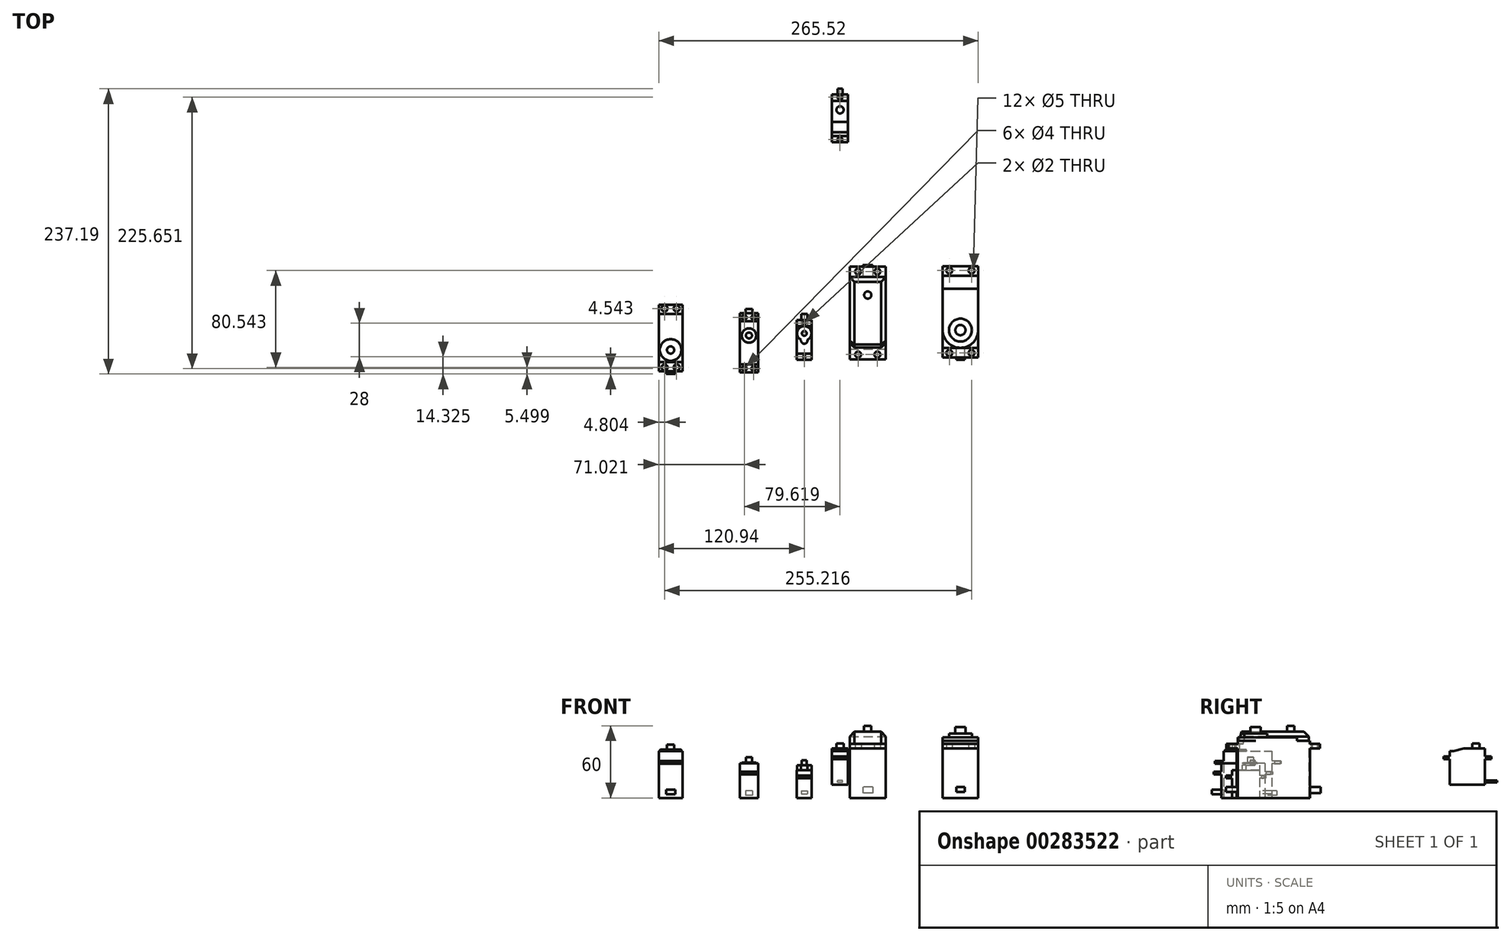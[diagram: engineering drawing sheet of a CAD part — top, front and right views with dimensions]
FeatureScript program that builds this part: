
annotation { "Feature Type Name" : "Feature", "Feature Type Description" : "" }
export const myFeature = defineFeature(function(context is Context, id is Id, definition is map)
    precondition{}
    {
        {
            var Q0;
            Q0=qCreatedBy(makeId("Top.planeOp"),FACE);
            var sketch = newSketch(context, id + "F0", { "sketchPlane" : qUnion([Q0])});
            skLineSegment(sketch, "E0.bottom", {"start": v(-143.99, -81.33) * mm, "end": v(-124.39, -81.33) * mm});
            skLineSegment(sketch, "E0.top", {"start": v(-143.99, -41.28) * mm, "end": v(-124.39, -41.28) * mm});
            skLineSegment(sketch, "E0.left", {"start": v(-143.99, -81.33) * mm, "end": v(-143.99, -41.28) * mm});
            skLineSegment(sketch, "E0.right", {"start": v(-124.39, -81.33) * mm, "end": v(-124.39, -41.28) * mm});
            skSolve(sketch);
        }
        {
            var Q0;
            Q0=makeQuery(id+"F0.imprint","IMPRINT",FACE,{"disambiguationData":[TD([[makeQuery(id+"F0.imprint","IMPRINT",EDGE,{"derivedFrom":sQuery(id+"F0.wireOp",EDGE,"E0.bottom")}),1.0]])]});
            extrude(context, id + "F1", {"entities" : qUnion([Q0]), "depth" : 28.3 * mm});
        }
        {
            var Q0;
            Q0=makeQuery(id+"F1.opExtrude","CAP_FACE",FACE,{"disambiguationData":[OSD([sQuery(id+"F0.wireOp",EDGE,"E0.bottom"),sQuery(id+"F0.wireOp",EDGE,"E0.top"),sQuery(id+"F0.wireOp",EDGE,"E0.left"),sQuery(id+"F0.wireOp",EDGE,"E0.right")])],"isStart":false});
            var sketch = newSketch(context, id + "F2", { "sketchPlane" : qUnion([Q0])});
            skLineSegment(sketch, "E1.bottom", {"start": v(-143.99, -33.78) * mm, "end": v(-124.39, -33.78) * mm});
            skLineSegment(sketch, "E1.top", {"start": v(-143.99, -88.83) * mm, "end": v(-124.39, -88.83) * mm});
            skLineSegment(sketch, "E1.left", {"start": v(-143.99, -33.78) * mm, "end": v(-143.99, -88.83) * mm});
            skLineSegment(sketch, "E1.right", {"start": v(-124.39, -33.78) * mm, "end": v(-124.39, -88.83) * mm});
            skCircle(sketch, "E2", {"center": v(-139.19, -36.78) * mm, "radius": 2.5 * mm});
            skCircle(sketch, "E3", {"center": v(-129.19, -36.78) * mm, "radius": 2.5 * mm});
            skCircle(sketch, "E4", {"center": v(-139.19, -85.83) * mm, "radius": 2.5 * mm});
            skCircle(sketch, "E5", {"center": v(-129.19, -85.83) * mm, "radius": 2.5 * mm});
            skLineSegment(sketch, "E6", {"start": v(-139.19, -85.83) * mm, "end": v(-129.19, -85.83) * mm, "construction": true});
            skLineSegment(sketch, "E7", {"start": v(-139.19, -36.78) * mm, "end": v(-129.19, -36.78) * mm, "construction": true});
            skLineSegment(sketch, "E8", {"start": v(-134.19, -36.78) * mm, "end": v(-134.19, -41.28) * mm, "construction": true});
            skLineSegment(sketch, "E9", {"start": v(-134.19, -85.83) * mm, "end": v(-134.19, -81.33) * mm, "construction": true});
            skSolve(sketch);
        }
        {
            var Q0;
            {var subQ1=makeQuery(id+"F1.opExtrude","CAP_EDGE",EDGE,{"disambiguationData":[OSD([sQuery(id+"F0.wireOp",EDGE,"E0.bottom")])],"isStart":false});Q0=makeQuery(id+"F2.imprint","IMPRINT",FACE,{"disambiguationData":[TD([[makeQuery(id+"F2.imprint","IMPRINT",EDGE,{"derivedFrom":subQ1}),1.0]])]});}
            extrude(context, id + "F3", {"entities" : qUnion([Q0]), "operationType" : NewBodyOperationType.ADD, "depth" : 10.5 * mm});
        }
        {
            var Q0;
            {var subQ2=sQuery(id+"F2.wireOp",EDGE,"E1.bottom");Q0=makeQuery(id+"F2.imprint","IMPRINT",FACE,{"disambiguationData":[TD([[makeQuery(id+"F2.imprint","IMPRINT",EDGE,{"derivedFrom":subQ2}),-1.0]])]});}
            var Q1;
            {var subQ2=sQuery(id+"F2.wireOp",EDGE,"E1.top");Q1=makeQuery(id+"F2.imprint","IMPRINT",FACE,{"disambiguationData":[TD([[makeQuery(id+"F2.imprint","IMPRINT",EDGE,{"derivedFrom":subQ2}),1.0]])]});}
            extrude(context, id + "F4", {"entities" : qUnion([Q0, Q1]), "operationType" : NewBodyOperationType.ADD, "depth" : 2.5 * mm});
        }
        {
            var Q0;
            Q0=makeQuery(id+"F3.opExtrude","CAP_FACE",FACE,{"disambiguationData":[OSD([sQuery(id+"F0.wireOp",EDGE,"E0.bottom"),sQuery(id+"F0.wireOp",EDGE,"E0.top"),sQuery(id+"F2.wireOp",EDGE,"E1.left"),sQuery(id+"F2.wireOp",EDGE,"E1.right")])],"isStart":false});
            var sketch = newSketch(context, id + "F5", { "sketchPlane" : qUnion([Q0])});
            skCircle(sketch, "E10", {"center": v(-134.19, -71.33) * mm, "radius": 9 * mm});
            skLineSegment(sketch, "E11", {"start": v(-134.19, -71.33) * mm, "end": v(-134.19, -81.33) * mm, "construction": true});
            skSolve(sketch);
        }
        {
            var Q0;
            Q0=makeQuery(id+"F5.imprint","IMPRINT",FACE,{"disambiguationData":[TD([[makeQuery(id+"F5.imprint","IMPRINT",EDGE,{"derivedFrom":sQuery(id+"F5.wireOp",EDGE,"E10")}),1.0]])]});
            extrude(context, id + "F6", {"entities" : qUnion([Q0]), "operationType" : NewBodyOperationType.ADD, "depth" : 1.5 * mm});
        }
        {
            var Q0;
            Q0=makeQuery(id+"F6.opExtrude","CAP_EDGE",EDGE,{"disambiguationData":[OSD([sQuery(id+"F5.wireOp",EDGE,"E10")])],"isStart":false});
            fillet(context, id + "F7", {"entities" : qUnion([Q0]), "radius" : 1 * mm, "tangentPropagation" : true, "allowEdgeOverflow" : false});
        }
        {
            var Q0;
            Q0=makeQuery(id+"F6.opExtrude","CAP_FACE",FACE,{"disambiguationData":[OSD([sQuery(id+"F5.wireOp",EDGE,"E10")])],"isStart":false});
            var sketch = newSketch(context, id + "F8", { "sketchPlane" : qUnion([Q0])});
            skCircle(sketch, "E12", {"center": v(-134.19, -71.33) * mm, "radius": 3 * mm});
            skSolve(sketch);
        }
        {
            var Q0;
            Q0=makeQuery(id+"F8.imprint","IMPRINT",FACE,{"disambiguationData":[TD([[makeQuery(id+"F8.imprint","IMPRINT",EDGE,{"derivedFrom":sQuery(id+"F8.wireOp",EDGE,"E12")}),1.0]])]});
            extrude(context, id + "F9", {"entities" : qUnion([Q0]), "operationType" : NewBodyOperationType.ADD, "depth" : 4 * mm});
        }
        {
            var Q0;
            {var subQ1=sQuery(id+"F0.wireOp",EDGE,"E0.right");var subQ2=sQuery(id+"F0.wireOp",EDGE,"E0.left");var subQ3=sQuery(id+"F0.wireOp",EDGE,"E0.top");var subQ4=sQuery(id+"F0.wireOp",EDGE,"E0.bottom");Q0=makeQuery(id+"F4.boolean.opBoolean","SPLIT",FACE,{"disambiguationData":[TD([makeQuery(id+"F1.opExtrude","CAP_FACE",FACE,{"disambiguationData":[OSD([subQ4,subQ3,subQ2,subQ1])],"isStart":true})])],"derivedFrom":makeQuery(id+"F3.boolean.opBoolean","MERGE",FACE,{"derivedFrom":[makeQuery(id+"F1.opExtrude","SWEPT_FACE",FACE,{"disambiguationData":[OSD([subQ4])]}),makeQuery(id+"F3.opExtrude","SWEPT_FACE",FACE,{"disambiguationData":[OSD([subQ4])]})]})});}
            var sketch = newSketch(context, id + "F10", { "sketchPlane" : qUnion([Q0])});
            skLineSegment(sketch, "E13.bottom", {"start": v(-137.94, 7) * mm, "end": v(-130.44, 7) * mm});
            skLineSegment(sketch, "E13.top", {"start": v(-137.94, 3) * mm, "end": v(-130.44, 3) * mm});
            skLineSegment(sketch, "E13.left", {"start": v(-137.94, 7) * mm, "end": v(-137.94, 3) * mm});
            skLineSegment(sketch, "E13.right", {"start": v(-130.44, 7) * mm, "end": v(-130.44, 3) * mm});
            skLineSegment(sketch, "E14", {"start": v(-134.19, 0) * mm, "end": v(-134.19, 3) * mm, "construction": true});
            skSolve(sketch);
        }
        {
            var Q0;
            Q0=makeQuery(id+"F10.imprint","IMPRINT",FACE,{"disambiguationData":[TD([[makeQuery(id+"F10.imprint","IMPRINT",EDGE,{"derivedFrom":sQuery(id+"F10.wireOp",EDGE,"E13.bottom")}),-1.0]])]});
            extrude(context, id + "F11", {"entities" : qUnion([Q0]), "operationType" : NewBodyOperationType.ADD, "depth" : 10 * mm});
        }
        {
            var Q0;
            Q0=qCreatedBy(makeId("Top.planeOp"),FACE);
            var sketch = newSketch(context, id + "F12", { "sketchPlane" : qUnion([Q0])});
            skLineSegment(sketch, "E15.bottom", {"start": v(-76.77, -47.29) * mm, "end": v(-61.27, -47.29) * mm});
            skLineSegment(sketch, "E15.top", {"start": v(-76.77, -83.29) * mm, "end": v(-61.27, -83.29) * mm});
            skLineSegment(sketch, "E15.left", {"start": v(-76.77, -47.29) * mm, "end": v(-76.77, -83.29) * mm});
            skLineSegment(sketch, "E15.right", {"start": v(-61.27, -47.29) * mm, "end": v(-61.27, -83.29) * mm});
            skSolve(sketch);
        }
        {
            var Q0;
            Q0=makeQuery(id+"F12.imprint","IMPRINT",FACE,{"disambiguationData":[TD([[makeQuery(id+"F12.imprint","IMPRINT",EDGE,{"derivedFrom":sQuery(id+"F12.wireOp",EDGE,"E15.bottom")}),-1.0]])]});
            extrude(context, id + "F13", {"entities" : qUnion([Q0]), "depth" : 19.5 * mm});
        }
        {
            var Q0;
            Q0=makeQuery(id+"F13.opExtrude","CAP_FACE",FACE,{"disambiguationData":[OSD([sQuery(id+"F12.wireOp",EDGE,"E15.bottom"),sQuery(id+"F12.wireOp",EDGE,"E15.top"),sQuery(id+"F12.wireOp",EDGE,"E15.left"),sQuery(id+"F12.wireOp",EDGE,"E15.right")])],"isStart":false});
            var sketch = newSketch(context, id + "F14", { "sketchPlane" : qUnion([Q0])});
            skLineSegment(sketch, "E16", {"start": v(-76.77, -47.29) * mm, "end": v(-76.77, -40.79) * mm});
            skLineSegment(sketch, "E17", {"start": v(-61.27, -47.29) * mm, "end": v(-61.27, -40.79) * mm});
            skLineSegment(sketch, "E18", {"start": v(-76.77, -40.79) * mm, "end": v(-61.27, -40.79) * mm});
            skLineSegment(sketch, "E19", {"start": v(-76.77, -83.29) * mm, "end": v(-76.77, -89.79) * mm});
            skLineSegment(sketch, "E20", {"start": v(-61.27, -83.29) * mm, "end": v(-61.27, -89.79) * mm});
            skLineSegment(sketch, "E21", {"start": v(-61.27, -89.79) * mm, "end": v(-76.77, -89.79) * mm});
            skCircle(sketch, "E22", {"center": v(-72.97, -44.29) * mm, "radius": 2 * mm});
            skCircle(sketch, "E23", {"center": v(-65.07, -44.29) * mm, "radius": 2 * mm});
            skCircle(sketch, "E24", {"center": v(-65.07, -86.79) * mm, "radius": 2 * mm});
            skCircle(sketch, "E25", {"center": v(-72.97, -86.79) * mm, "radius": 2 * mm});
            skLineSegment(sketch, "E26", {"start": v(-76.77, -44.29) * mm, "end": v(-61.27, -44.29) * mm, "construction": true});
            skLineSegment(sketch, "E27", {"start": v(-72.97, -40.79) * mm, "end": v(-72.97, -47.29) * mm, "construction": true});
            skLineSegment(sketch, "E28", {"start": v(-65.07, -40.79) * mm, "end": v(-65.07, -47.29) * mm, "construction": true});
            skLineSegment(sketch, "E29", {"start": v(-76.77, -86.79) * mm, "end": v(-61.27, -86.79) * mm, "construction": true});
            skLineSegment(sketch, "E30", {"start": v(-72.97, -83.29) * mm, "end": v(-72.97, -89.79) * mm, "construction": true});
            skLineSegment(sketch, "E31", {"start": v(-65.07, -83.29) * mm, "end": v(-65.07, -89.79) * mm, "construction": true});
            skSolve(sketch);
        }
        {
            var Q0;
            Q0=makeQuery(id+"F14.imprint","IMPRINT",FACE,{"disambiguationData":[TD([[makeQuery(id+"F14.imprint","IMPRINT",EDGE,{"derivedFrom":makeQuery(id+"F13.opExtrude","CAP_EDGE",EDGE,{"disambiguationData":[OSD([sQuery(id+"F12.wireOp",EDGE,"E15.bottom")])],"isStart":false})}),-1.0]])]});
            var Q1;
            Q1=makeQuery(id+"F14.imprint","IMPRINT",FACE,{"disambiguationData":[TD([[makeQuery(id+"F14.imprint","IMPRINT",EDGE,{"derivedFrom":sQuery(id+"F14.wireOp",EDGE,"E19")}),1.0]])]});
            var Q2;
            Q2=makeQuery(id+"F14.imprint","IMPRINT",FACE,{"disambiguationData":[TD([[makeQuery(id+"F14.imprint","IMPRINT",EDGE,{"derivedFrom":sQuery(id+"F14.wireOp",EDGE,"E16")}),-1.0]])]});
            extrude(context, id + "F15", {"entities" : qUnion([Q0, Q1, Q2]), "operationType" : NewBodyOperationType.ADD, "depth" : 2.4 * mm});
        }
        {
            var Q0;
            Q0=makeQuery(id+"F15.opExtrude","CAP_FACE",FACE,{"disambiguationData":[OSD([sQuery(id+"F12.wireOp",EDGE,"E15.left"),sQuery(id+"F12.wireOp",EDGE,"E15.right"),sQuery(id+"F14.wireOp",EDGE,"E16"),sQuery(id+"F14.wireOp",EDGE,"E17"),sQuery(id+"F14.wireOp",EDGE,"E18"),sQuery(id+"F14.wireOp",EDGE,"E19"),sQuery(id+"F14.wireOp",EDGE,"E20"),sQuery(id+"F14.wireOp",EDGE,"E21"),sQuery(id+"F14.wireOp",EDGE,"E22"),sQuery(id+"F14.wireOp",EDGE,"E23"),sQuery(id+"F14.wireOp",EDGE,"E24"),sQuery(id+"F14.wireOp",EDGE,"E25")])],"isStart":false});
            var sketch = newSketch(context, id + "F16", { "sketchPlane" : qUnion([Q0])});
            skLineSegment(sketch, "E32", {"start": v(-76.77, -83.29) * mm, "end": v(-61.27, -83.29) * mm});
            skLineSegment(sketch, "E33", {"start": v(-61.27, -47.29) * mm, "end": v(-76.77, -47.29) * mm});
            skSolve(sketch);
        }
        {
            var Q0;
            {var subQ0=sQuery(id+"F16.wireOp",EDGE,"E32");Q0=makeQuery(id+"F16.imprint","IMPRINT",FACE,{"disambiguationData":[TD([[makeQuery(id+"F16.imprint","IMPRINT",EDGE,{"derivedFrom":subQ0}),1.0]])]});}
            extrude(context, id + "F17", {"entities" : qUnion([Q0]), "operationType" : NewBodyOperationType.ADD, "depth" : 7 * mm});
        }
        {
            var Q0;
            Q0=makeQuery(id+"F17.opExtrude","CAP_FACE",FACE,{"disambiguationData":[OSD([sQuery(id+"F12.wireOp",EDGE,"E15.left"),sQuery(id+"F12.wireOp",EDGE,"E15.right"),sQuery(id+"F14.wireOp",EDGE,"E16"),sQuery(id+"F14.wireOp",EDGE,"E17"),sQuery(id+"F14.wireOp",EDGE,"E19"),sQuery(id+"F14.wireOp",EDGE,"E20"),sQuery(id+"F16.wireOp",EDGE,"E32"),sQuery(id+"F16.wireOp",EDGE,"E33")])],"isStart":false});
            var sketch = newSketch(context, id + "F18", { "sketchPlane" : qUnion([Q0])});
            skCircle(sketch, "E34", {"center": v(-69.02, -59.29) * mm, "radius": 6 * mm});
            skLineSegment(sketch, "E35", {"start": v(-69.02, -47.29) * mm, "end": v(-69.02, -59.29) * mm, "construction": true});
            skSolve(sketch);
        }
        {
            var Q0;
            Q0=makeQuery(id+"F18.imprint","IMPRINT",FACE,{"disambiguationData":[TD([[makeQuery(id+"F18.imprint","IMPRINT",EDGE,{"derivedFrom":sQuery(id+"F18.wireOp",EDGE,"E34")}),1.0]])]});
            extrude(context, id + "F19", {"entities" : qUnion([Q0]), "operationType" : NewBodyOperationType.ADD, "depth" : 0.65 * mm});
        }
        {
            var Q0;
            Q0=makeQuery(id+"F19.opExtrude","CAP_EDGE",EDGE,{"disambiguationData":[OSD([sQuery(id+"F18.wireOp",EDGE,"E34")])],"isStart":false});
            fillet(context, id + "F20", {"entities" : qUnion([Q0]), "radius" : 1 * mm, "tangentPropagation" : true, "allowEdgeOverflow" : false});
        }
        {
            var Q0;
            Q0=makeQuery(id+"F19.opExtrude","CAP_FACE",FACE,{"disambiguationData":[OSD([sQuery(id+"F18.wireOp",EDGE,"E34")])],"isStart":false});
            var sketch = newSketch(context, id + "F21", { "sketchPlane" : qUnion([Q0])});
            skCircle(sketch, "E36", {"center": v(-69.02, -59.29) * mm, "radius": 2.5 * mm});
            skSolve(sketch);
        }
        {
            var Q0;
            Q0=makeQuery(id+"F21.imprint","IMPRINT",FACE,{"disambiguationData":[TD([[makeQuery(id+"F21.imprint","IMPRINT",EDGE,{"derivedFrom":sQuery(id+"F21.wireOp",EDGE,"E36")}),1.0]])]});
            extrude(context, id + "F22", {"entities" : qUnion([Q0]), "operationType" : NewBodyOperationType.ADD, "depth" : 4.2 * mm});
        }
        {
            var Q0;
            Q0=makeQuery(id+"F13.opExtrude","SWEPT_FACE",FACE,{"disambiguationData":[OSD([sQuery(id+"F12.wireOp",EDGE,"E15.bottom")])]});
            var sketch = newSketch(context, id + "F23", { "sketchPlane" : qUnion([Q0])});
            skLineSegment(sketch, "E37.bottom", {"start": v(66.02, 6) * mm, "end": v(72.02, 6) * mm});
            skLineSegment(sketch, "E37.top", {"start": v(66.02, 2) * mm, "end": v(72.02, 2) * mm});
            skLineSegment(sketch, "E37.left", {"start": v(66.02, 6) * mm, "end": v(66.02, 2) * mm});
            skLineSegment(sketch, "E37.right", {"start": v(72.02, 6) * mm, "end": v(72.02, 2) * mm});
            skLineSegment(sketch, "E38", {"start": v(69.02, 0) * mm, "end": v(69.02, 6) * mm, "construction": true});
            skSolve(sketch);
        }
        {
            var Q0;
            Q0=makeQuery(id+"F23.imprint","IMPRINT",FACE,{"disambiguationData":[TD([[makeQuery(id+"F23.imprint","IMPRINT",EDGE,{"derivedFrom":sQuery(id+"F23.wireOp",EDGE,"E37.bottom")}),-1.0]])]});
            extrude(context, id + "F24", {"entities" : qUnion([Q0]), "operationType" : NewBodyOperationType.ADD, "depth" : 10 * mm});
        }
        {
            var Q0;
            Q0=qCreatedBy(makeId("Top.planeOp"),FACE);
            var sketch = newSketch(context, id + "F25", { "sketchPlane" : qUnion([Q0])});
            skLineSegment(sketch, "E39.bottom", {"start": v(-29.3, -74.5) * mm, "end": v(-16.8, -74.5) * mm});
            skLineSegment(sketch, "E39.top", {"start": v(-29.3, -51.5) * mm, "end": v(-16.8, -51.5) * mm});
            skLineSegment(sketch, "E39.left", {"start": v(-29.3, -74.5) * mm, "end": v(-29.3, -51.5) * mm});
            skLineSegment(sketch, "E39.right", {"start": v(-16.8, -74.5) * mm, "end": v(-16.8, -51.5) * mm});
            skSolve(sketch);
        }
        {
            var Q0;
            Q0=makeQuery(id+"F25.imprint","IMPRINT",FACE,{"disambiguationData":[TD([[makeQuery(id+"F25.imprint","IMPRINT",EDGE,{"derivedFrom":sQuery(id+"F25.wireOp",EDGE,"E39.bottom")}),1.0]])]});
            extrude(context, id + "F26", {"entities" : qUnion([Q0]), "depth" : 16.5 * mm});
        }
        {
            var Q0;
            Q0=makeQuery(id+"F26.opExtrude","CAP_FACE",FACE,{"disambiguationData":[OSD([sQuery(id+"F25.wireOp",EDGE,"E39.bottom"),sQuery(id+"F25.wireOp",EDGE,"E39.top"),sQuery(id+"F25.wireOp",EDGE,"E39.left"),sQuery(id+"F25.wireOp",EDGE,"E39.right")])],"isStart":false});
            var sketch = newSketch(context, id + "F27", { "sketchPlane" : qUnion([Q0])});
            skLineSegment(sketch, "E40", {"start": v(-29.3, -51.5) * mm, "end": v(-29.3, -46.5) * mm});
            skLineSegment(sketch, "E41", {"start": v(-29.3, -46.5) * mm, "end": v(-16.8, -46.5) * mm});
            skLineSegment(sketch, "E42", {"start": v(-16.8, -46.5) * mm, "end": v(-16.8, -51.5) * mm});
            skLineSegment(sketch, "E43", {"start": v(-29.3, -74.5) * mm, "end": v(-29.3, -79.5) * mm});
            skLineSegment(sketch, "E44", {"start": v(-29.3, -79.5) * mm, "end": v(-16.8, -79.5) * mm});
            skLineSegment(sketch, "E45", {"start": v(-16.8, -79.5) * mm, "end": v(-16.8, -74.5) * mm});
            skLineSegment(sketch, "E46", {"start": v(-29.3, -49) * mm, "end": v(-16.8, -49) * mm, "construction": true});
            skLineSegment(sketch, "E47", {"start": v(-23.05, -49) * mm, "end": v(-23.05, -46.5) * mm, "construction": true});
            skLineSegment(sketch, "E48", {"start": v(-29.3, -77) * mm, "end": v(-16.8, -77) * mm, "construction": true});
            skLineSegment(sketch, "E49", {"start": v(-23.05, -77) * mm, "end": v(-23.05, -79.5) * mm, "construction": true});
            skCircle(sketch, "E50", {"center": v(-23.05, -49) * mm, "radius": 1 * mm});
            skCircle(sketch, "E51", {"center": v(-23.05, -77) * mm, "radius": 1 * mm});
            skSolve(sketch);
        }
        {
            var Q0;
            Q0=makeQuery(id+"F27.imprint","IMPRINT",FACE,{"disambiguationData":[TD([[makeQuery(id+"F27.imprint","IMPRINT",EDGE,{"derivedFrom":sQuery(id+"F27.wireOp",EDGE,"E43")}),1.0]])]});
            var Q1;
            Q1=makeQuery(id+"F27.imprint","IMPRINT",FACE,{"disambiguationData":[TD([[makeQuery(id+"F27.imprint","IMPRINT",EDGE,{"derivedFrom":makeQuery(id+"F26.opExtrude","CAP_EDGE",EDGE,{"disambiguationData":[OSD([sQuery(id+"F25.wireOp",EDGE,"E39.bottom")])],"isStart":false})}),1.0]])]});
            var Q2;
            Q2=makeQuery(id+"F27.imprint","IMPRINT",FACE,{"disambiguationData":[TD([[makeQuery(id+"F27.imprint","IMPRINT",EDGE,{"derivedFrom":sQuery(id+"F27.wireOp",EDGE,"E40")}),-1.0]])]});
            extrude(context, id + "F28", {"entities" : qUnion([Q0, Q1, Q2]), "operationType" : NewBodyOperationType.ADD, "depth" : 2.2 * mm});
        }
        {
            var Q0;
            Q0=makeQuery(id+"F28.opExtrude","CAP_FACE",FACE,{"disambiguationData":[OSD([sQuery(id+"F25.wireOp",EDGE,"E39.left"),sQuery(id+"F25.wireOp",EDGE,"E39.right"),sQuery(id+"F27.wireOp",EDGE,"E40"),sQuery(id+"F27.wireOp",EDGE,"E41"),sQuery(id+"F27.wireOp",EDGE,"E42"),sQuery(id+"F27.wireOp",EDGE,"E43"),sQuery(id+"F27.wireOp",EDGE,"E44"),sQuery(id+"F27.wireOp",EDGE,"E45"),sQuery(id+"F27.wireOp",EDGE,"E50"),sQuery(id+"F27.wireOp",EDGE,"E51")])],"isStart":false});
            var sketch = newSketch(context, id + "F29", { "sketchPlane" : qUnion([Q0])});
            skLineSegment(sketch, "E52", {"start": v(-29.3, -51.5) * mm, "end": v(-16.8, -51.5) * mm});
            skLineSegment(sketch, "E53", {"start": v(-16.8, -74.5) * mm, "end": v(-29.3, -74.5) * mm});
            skSolve(sketch);
        }
        {
            var Q0;
            {var subQ0=sQuery(id+"F29.wireOp",EDGE,"E52");Q0=makeQuery(id+"F29.imprint","IMPRINT",FACE,{"disambiguationData":[TD([[makeQuery(id+"F29.imprint","IMPRINT",EDGE,{"derivedFrom":subQ0}),-1.0]])]});}
            extrude(context, id + "F30", {"entities" : qUnion([Q0]), "operationType" : NewBodyOperationType.ADD, "depth" : 4.5 * mm});
        }
        {
            var Q0;
            Q0=makeQuery(id+"F30.opExtrude","CAP_FACE",FACE,{"disambiguationData":[OSD([sQuery(id+"F25.wireOp",EDGE,"E39.left"),sQuery(id+"F25.wireOp",EDGE,"E39.right"),sQuery(id+"F27.wireOp",EDGE,"E40"),sQuery(id+"F27.wireOp",EDGE,"E42"),sQuery(id+"F27.wireOp",EDGE,"E43"),sQuery(id+"F27.wireOp",EDGE,"E45"),sQuery(id+"F29.wireOp",EDGE,"E52"),sQuery(id+"F29.wireOp",EDGE,"E53")])],"isStart":false});
            var sketch = newSketch(context, id + "F31", { "sketchPlane" : qUnion([Q0])});
            skArc(sketch, "E54", {"start": v(-20.47, -62.92) * mm, "mid": v(-23.05, -51.5) * mm, "end": v(-25.63, -62.92) * mm});
            skLineSegment(sketch, "E55", {"start": v(-23.05, -57.5) * mm, "end": v(-23.05, -51.5) * mm, "construction": true});
            skLineSegment(sketch, "E56", {"start": v(-23.05, -57.5) * mm, "end": v(-23.05, -63.5) * mm, "construction": true});
            skArc(sketch, "E57", {"start": v(-25.63, -62.92) * mm, "mid": v(-23.05, -66.16) * mm, "end": v(-20.47, -62.92) * mm});
            skSolve(sketch);
        }
        {
            var Q0;
            {var subQ0=sQuery(id+"F31.wireOp",EDGE,"E57");Q0=makeQuery(id+"F31.imprint","IMPRINT",FACE,{"disambiguationData":[TD([[makeQuery(id+"F31.imprint","IMPRINT",EDGE,{"derivedFrom":subQ0}),1.0]])]});}
            extrude(context, id + "F32", {"entities" : qUnion([Q0]), "operationType" : NewBodyOperationType.ADD, "depth" : 4 * mm});
        }
        {
            var Q0;
            Q0=makeQuery(id+"F32.opExtrude","CAP_FACE",FACE,{"disambiguationData":[OSD([sQuery(id+"F31.wireOp",EDGE,"E54"),sQuery(id+"F31.wireOp",EDGE,"E57")])],"isStart":false});
            var sketch = newSketch(context, id + "F33", { "sketchPlane" : qUnion([Q0])});
            skCircle(sketch, "E58", {"center": v(-23.05, -57.5) * mm, "radius": 2 * mm});
            skSolve(sketch);
        }
        {
            var Q0;
            Q0=makeQuery(id+"F33.imprint","IMPRINT",FACE,{"disambiguationData":[TD([[makeQuery(id+"F33.imprint","IMPRINT",EDGE,{"derivedFrom":sQuery(id+"F33.wireOp",EDGE,"E58")}),1.0]])]});
            extrude(context, id + "F34", {"entities" : qUnion([Q0]), "operationType" : NewBodyOperationType.ADD, "depth" : 4 * mm});
        }
        {
            var Q0;
            Q0=makeQuery(id+"F26.opExtrude","SWEPT_FACE",FACE,{"disambiguationData":[OSD([sQuery(id+"F25.wireOp",EDGE,"E39.top")])]});
            var sketch = newSketch(context, id + "F35", { "sketchPlane" : qUnion([Q0])});
            skLineSegment(sketch, "E59.bottom", {"start": v(25.55, 6) * mm, "end": v(20.55, 6) * mm});
            skLineSegment(sketch, "E59.top", {"start": v(25.55, 3.5) * mm, "end": v(20.55, 3.5) * mm});
            skLineSegment(sketch, "E59.left", {"start": v(25.55, 6) * mm, "end": v(25.55, 3.5) * mm});
            skLineSegment(sketch, "E59.right", {"start": v(20.55, 6) * mm, "end": v(20.55, 3.5) * mm});
            skLineSegment(sketch, "E60", {"start": v(23.05, 6) * mm, "end": v(23.05, 0) * mm, "construction": true});
            skSolve(sketch);
        }
        {
            var Q0;
            Q0=makeQuery(id+"F35.imprint","IMPRINT",FACE,{"disambiguationData":[TD([[makeQuery(id+"F35.imprint","IMPRINT",EDGE,{"derivedFrom":sQuery(id+"F35.wireOp",EDGE,"E59.bottom")}),1.0]])]});
            extrude(context, id + "F36", {"entities" : qUnion([Q0]), "operationType" : NewBodyOperationType.ADD, "depth" : 10 * mm});
        }
        {
            var Q0;
            Q0=qCreatedBy(makeId("Right.planeOp"),FACE);
            var sketch = newSketch(context, id + "F37", { "sketchPlane" : qUnion([Q0])});
            skLineSegment(sketch, "E61.bottom", {"start": v(106.66, 10.85) * mm, "end": v(135.86, 10.85) * mm});
            skLineSegment(sketch, "E61.top", {"start": v(118.36, 41.15) * mm, "end": v(135.86, 41.15) * mm});
            skLineSegment(sketch, "E61.left", {"start": v(106.66, 10.85) * mm, "end": v(106.66, 32.35) * mm});
            skLineSegment(sketch, "E61.right", {"start": v(135.86, 10.85) * mm, "end": v(135.86, 32.35) * mm});
            skLineSegment(sketch, "E62.bottom", {"start": v(135.86, 32.35) * mm, "end": v(141.11, 32.35) * mm});
            skLineSegment(sketch, "E62.top", {"start": v(135.86, 34.35) * mm, "end": v(141.11, 34.35) * mm});
            skLineSegment(sketch, "E62.right", {"start": v(141.11, 32.35) * mm, "end": v(141.11, 34.35) * mm});
            skLineSegment(sketch, "E63.bottom", {"start": v(106.66, 34.35) * mm, "end": v(101.41, 34.35) * mm});
            skLineSegment(sketch, "E63.top", {"start": v(106.66, 32.35) * mm, "end": v(101.41, 32.35) * mm});
            skLineSegment(sketch, "E63.right", {"start": v(101.41, 34.35) * mm, "end": v(101.41, 32.35) * mm});
            skLineSegment(sketch, "E64", {"start": v(135.86, 32.35) * mm, "end": v(106.66, 32.35) * mm, "construction": true});
            skLineSegment(sketch, "E65", {"start": v(106.66, 34.35) * mm, "end": v(135.86, 34.35) * mm, "construction": true});
            skLineSegment(sketch, "E66", {"start": v(106.66, 38.85) * mm, "end": v(109.66, 38.85) * mm});
            skLineSegment(sketch, "E67", {"start": v(109.66, 38.85) * mm, "end": v(118.36, 41.15) * mm});
            skLineSegment(sketch, "E68.trimOffspring", {"start": v(106.66, 34.35) * mm, "end": v(106.66, 38.85) * mm});
            skLineSegment(sketch, "E69.trimOffspring", {"start": v(135.86, 34.35) * mm, "end": v(135.86, 41.15) * mm});
            skSolve(sketch);
        }
        {
            var Q0;
            Q0=makeQuery(id+"F37.imprint","IMPRINT",FACE,{"disambiguationData":[TD([[makeQuery(id+"F37.imprint","IMPRINT",EDGE,{"derivedFrom":sQuery(id+"F37.wireOp",EDGE,"E61.bottom")}),1.0]])]});
            extrude(context, id + "F38", {"entities" : qUnion([Q0]), "depth" : 13.3 * mm});
        }
        {
            var Q0;
            Q0=makeQuery(id+"F38.opExtrude","SWEPT_FACE",FACE,{"disambiguationData":[OSD([sQuery(id+"F37.wireOp",EDGE,"E61.top")])]});
            var sketch = newSketch(context, id + "F39", { "sketchPlane" : qUnion([Q0])});
            skCircle(sketch, "E70", {"center": v(6.65, 128.36) * mm, "radius": 3 * mm});
            skLineSegment(sketch, "E71", {"start": v(6.65, 135.86) * mm, "end": v(6.65, 128.36) * mm, "construction": true});
            skSolve(sketch);
        }
        {
            var Q0;
            Q0=makeQuery(id+"F39.imprint","IMPRINT",FACE,{"disambiguationData":[TD([[makeQuery(id+"F39.imprint","IMPRINT",EDGE,{"derivedFrom":sQuery(id+"F39.wireOp",EDGE,"E70")}),1.0]])]});
            extrude(context, id + "F40", {"entities" : qUnion([Q0]), "operationType" : NewBodyOperationType.ADD, "depth" : 4 * mm});
        }
        {
            var Q0;
            Q0=makeQuery(id+"F38.opExtrude","SWEPT_FACE",FACE,{"disambiguationData":[OSD([sQuery(id+"F37.wireOp",EDGE,"E63.bottom")])]});
            var sketch = newSketch(context, id + "F41", { "sketchPlane" : qUnion([Q0])});
            skLineSegment(sketch, "E72", {"start": v(6.65, 101.41) * mm, "end": v(6.65, 106.66) * mm, "construction": true});
            skLineSegment(sketch, "E73", {"start": v(6.65, 141.11) * mm, "end": v(6.65, 136.02) * mm, "construction": true});
            skCircle(sketch, "E74", {"center": v(6.65, 138.86) * mm, "radius": 2 * mm});
            skCircle(sketch, "E75", {"center": v(6.65, 103.66) * mm, "radius": 2 * mm});
            skSolve(sketch);
        }
        {
            var Q0;
            Q0=makeQuery(id+"F41.imprint","IMPRINT",FACE,{"disambiguationData":[TD([[makeQuery(id+"F41.imprint","IMPRINT",EDGE,{"derivedFrom":sQuery(id+"F41.wireOp",EDGE,"E75")}),1.0]])]});
            var Q1;
            Q1=makeQuery(id+"F41.imprint","IMPRINT",FACE,{"disambiguationData":[TD([[makeQuery(id+"F41.imprint","IMPRINT",EDGE,{"derivedFrom":sQuery(id+"F41.wireOp",EDGE,"E74")}),1.0]])]});
            extrude(context, id + "F42", {"entities" : qUnion([Q0, Q1]), "operationType" : NewBodyOperationType.REMOVE, "endBound" : BoundingType.THROUGH_ALL, "oppositeDirection" : true, "depth" : 25 * mm});
        }
        {
            var Q0;
            Q0=makeQuery(id+"F38.opExtrude","SWEPT_FACE",FACE,{"disambiguationData":[OSD([sQuery(id+"F37.wireOp",EDGE,"E61.right")])]});
            var sketch = newSketch(context, id + "F43", { "sketchPlane" : qUnion([Q0])});
            skLineSegment(sketch, "E76.bottom", {"start": v(-8.65, 12.85) * mm, "end": v(-4.65, 12.85) * mm});
            skLineSegment(sketch, "E76.top", {"start": v(-8.65, 14.35) * mm, "end": v(-4.65, 14.35) * mm});
            skLineSegment(sketch, "E76.left", {"start": v(-8.65, 12.85) * mm, "end": v(-8.65, 14.35) * mm});
            skLineSegment(sketch, "E76.right", {"start": v(-4.65, 12.85) * mm, "end": v(-4.65, 14.35) * mm});
            skLineSegment(sketch, "E77", {"start": v(-6.65, 10.85) * mm, "end": v(-6.65, 12.85) * mm, "construction": true});
            skSolve(sketch);
        }
        {
            var Q0;
            Q0=makeQuery(id+"F43.imprint","IMPRINT",FACE,{"disambiguationData":[TD([[makeQuery(id+"F43.imprint","IMPRINT",EDGE,{"derivedFrom":sQuery(id+"F43.wireOp",EDGE,"E76.bottom")}),1.0]])]});
            extrude(context, id + "F44", {"entities" : qUnion([Q0]), "operationType" : NewBodyOperationType.ADD, "depth" : 10 * mm});
        }
        {
            var Q0;
            Q0=qCreatedBy(makeId("Top.planeOp"),FACE);
            var sketch = newSketch(context, id + "F45", { "sketchPlane" : qUnion([Q0])});
            skLineSegment(sketch, "E78.bottom", {"start": v(14.71, -70.64) * mm, "end": v(44.71, -70.64) * mm});
            skLineSegment(sketch, "E78.top", {"start": v(14.71, -10.64) * mm, "end": v(44.71, -10.64) * mm});
            skLineSegment(sketch, "E78.left", {"start": v(14.71, -70.64) * mm, "end": v(14.71, -10.64) * mm});
            skLineSegment(sketch, "E78.right", {"start": v(44.71, -70.64) * mm, "end": v(44.71, -10.64) * mm});
            skSolve(sketch);
        }
        {
            var Q0;
            Q0=makeQuery(id+"F45.imprint","IMPRINT",FACE,{"disambiguationData":[TD([[makeQuery(id+"F45.imprint","IMPRINT",EDGE,{"derivedFrom":sQuery(id+"F45.wireOp",EDGE,"E78.bottom")}),1.0]])]});
            extrude(context, id + "F46", {"entities" : qUnion([Q0]), "depth" : 41 * mm, "offsetDistance" : 25 * mm});
        }
        {
            var Q0;
            Q0=makeQuery(id+"F46.opExtrude","CAP_FACE",FACE,{"disambiguationData":[OSD([sQuery(id+"F45.wireOp",EDGE,"E78.bottom"),sQuery(id+"F45.wireOp",EDGE,"E78.top"),sQuery(id+"F45.wireOp",EDGE,"E78.left"),sQuery(id+"F45.wireOp",EDGE,"E78.right")])],"isStart":false});
            var sketch = newSketch(context, id + "F47", { "sketchPlane" : qUnion([Q0])});
            skLineSegment(sketch, "E79.bottom", {"start": v(14.71, -79.14) * mm, "end": v(44.71, -79.14) * mm});
            skLineSegment(sketch, "E79.top", {"start": v(14.71, -2.14) * mm, "end": v(44.71, -2.14) * mm});
            skLineSegment(sketch, "E79.left", {"start": v(14.71, -79.14) * mm, "end": v(14.71, -2.14) * mm});
            skLineSegment(sketch, "E79.right", {"start": v(44.71, -79.14) * mm, "end": v(44.71, -2.14) * mm});
            skCircle(sketch, "E80", {"center": v(21.71, -75.14) * mm, "radius": 2.5 * mm});
            skCircle(sketch, "E81", {"center": v(37.71, -75.14) * mm, "radius": 2.5 * mm});
            skCircle(sketch, "E82", {"center": v(21.71, -6.14) * mm, "radius": 2.5 * mm});
            skCircle(sketch, "E83", {"center": v(37.71, -6.14) * mm, "radius": 2.5 * mm});
            skLineSegment(sketch, "E84", {"start": v(21.71, -75.14) * mm, "end": v(37.71, -75.14) * mm, "construction": true});
            skLineSegment(sketch, "E85", {"start": v(37.71, -6.14) * mm, "end": v(37.71, -75.14) * mm, "construction": true});
            skLineSegment(sketch, "E86", {"start": v(37.71, -6.14) * mm, "end": v(21.71, -6.14) * mm, "construction": true});
            skLineSegment(sketch, "E87", {"start": v(21.71, -6.14) * mm, "end": v(21.71, -75.14) * mm, "construction": true});
            skSolve(sketch);
        }
        {
            var Q0;
            {var subQ1=makeQuery(id+"F46.opExtrude","CAP_EDGE",EDGE,{"disambiguationData":[OSD([sQuery(id+"F45.wireOp",EDGE,"E78.bottom")])],"isStart":false});Q0=makeQuery(id+"F47.imprint","IMPRINT",FACE,{"disambiguationData":[TD([[makeQuery(id+"F47.imprint","IMPRINT",EDGE,{"derivedFrom":subQ1}),1.0]])]});}
            extrude(context, id + "F48", {"entities" : qUnion([Q0]), "operationType" : NewBodyOperationType.ADD, "depth" : 14 * mm, "offsetDistance" : 25 * mm});
        }
        {
            var Q0;
            {var subQ0=sQuery(id+"F47.wireOp",EDGE,"E79.bottom");Q0=makeQuery(id+"F47.imprint","IMPRINT",FACE,{"disambiguationData":[TD([[makeQuery(id+"F47.imprint","IMPRINT",EDGE,{"derivedFrom":subQ0}),1.0]])]});}
            var Q1;
            {var subQ0=sQuery(id+"F47.wireOp",EDGE,"E79.top");Q1=makeQuery(id+"F47.imprint","IMPRINT",FACE,{"disambiguationData":[TD([[makeQuery(id+"F47.imprint","IMPRINT",EDGE,{"derivedFrom":subQ0}),-1.0]])]});}
            extrude(context, id + "F49", {"entities" : qUnion([Q0, Q1]), "operationType" : NewBodyOperationType.ADD, "depth" : 4 * mm, "offsetDistance" : 25 * mm});
        }
        {
            var Q0;
            Q0=makeQuery(id+"F48.opExtrude","CAP_FACE",FACE,{"disambiguationData":[OSD([sQuery(id+"F45.wireOp",EDGE,"E78.bottom"),sQuery(id+"F45.wireOp",EDGE,"E78.top"),sQuery(id+"F47.wireOp",EDGE,"E79.left"),sQuery(id+"F47.wireOp",EDGE,"E79.right")])],"isStart":false});
            var sketch = newSketch(context, id + "F50", { "sketchPlane" : qUnion([Q0])});
            skLineSegment(sketch, "E88", {"start": v(14.71, -25.64) * mm, "end": v(44.71, -25.64) * mm, "construction": true});
            skLineSegment(sketch, "E89", {"start": v(29.71, -25.64) * mm, "end": v(29.71, -10.64) * mm, "construction": true});
            skCircle(sketch, "E90", {"center": v(29.71, -25.64) * mm, "radius": 3 * mm});
            skSolve(sketch);
        }
        {
            var Q0;
            Q0=makeQuery(id+"F50.imprint","IMPRINT",FACE,{"disambiguationData":[TD([[makeQuery(id+"F50.imprint","IMPRINT",EDGE,{"derivedFrom":sQuery(id+"F50.wireOp",EDGE,"E90")}),1.0]])]});
            extrude(context, id + "F51", {"entities" : qUnion([Q0]), "operationType" : NewBodyOperationType.ADD, "depth" : 5 * mm, "offsetDistance" : 25 * mm});
        }
        {
            var Q0;
            Q0=makeQuery(id+"F48.opExtrude","CAP_EDGE",EDGE,{"disambiguationData":[OSD([sQuery(id+"F45.wireOp",EDGE,"E78.bottom")])],"isStart":false});
            chamfer(context, id + "F52", {"entities" : qUnion([Q0]), "chamferType" : ChamferType.TWO_OFFSETS, "width1" : 15 * mm, "oppositeDirection" : false, "width2" : 4 * mm, "tangentPropagation" : true});
        }
        {
            var Q0;
            {var subQ0=sQuery(id+"F47.wireOp",EDGE,"E79.right");var subQ1=sQuery(id+"F45.wireOp",EDGE,"E78.bottom");Q0=makeQuery(id+"F52.opChamfer","BLEND_EDGE",EDGE,{"blendedFrom":[makeQuery(id+"F48.opExtrude","CAP_EDGE",EDGE,{"disambiguationData":[OSD([subQ1])],"isStart":false}),makeQuery(id+"F49.boolean.opBoolean","MERGE",FACE,{"derivedFrom":[makeQuery(id+"F48.boolean.opBoolean","MERGE",FACE,{"derivedFrom":[makeQuery(id+"F46.opExtrude","SWEPT_FACE",FACE,{"disambiguationData":[OSD([sQuery(id+"F45.wireOp",EDGE,"E78.right")])]}),makeQuery(id+"F48.opExtrude","SWEPT_FACE",FACE,{"disambiguationData":[OSD([subQ0])]})]}),makeQuery(id+"F49.opExtrude","SWEPT_FACE",FACE,{"disambiguationData":[OSD([subQ0]),TDD([makeQuery(id+"F47.imprint","IMPRINT",EDGE,{"disambiguationData":[TD([[makeQuery(id+"F47.imprint","INTERSECT",VERTEX,{"derivedFrom":[makeQuery(id+"F46.opExtrude","CAP_EDGE",EDGE,{"disambiguationData":[OSD([subQ1])],"isStart":false}),subQ0]}),1.0]])],"derivedFrom":subQ0})])]}),makeQuery(id+"F49.opExtrude","SWEPT_FACE",FACE,{"disambiguationData":[OSD([subQ0]),TDD([makeQuery(id+"F47.imprint","IMPRINT",EDGE,{"disambiguationData":[TD([[makeQuery(id+"F47.imprint","INTERSECT",VERTEX,{"derivedFrom":[makeQuery(id+"F46.opExtrude","CAP_EDGE",EDGE,{"disambiguationData":[OSD([sQuery(id+"F45.wireOp",EDGE,"E78.top")])],"isStart":false}),subQ0]}),-1.0]])],"derivedFrom":subQ0})])]})]})],"blendedInto":[makeQuery(id+"F49.boolean.opBoolean","MERGE",FACE,{"derivedFrom":[makeQuery(id+"F48.boolean.opBoolean","MERGE",FACE,{"derivedFrom":[makeQuery(id+"F46.opExtrude","SWEPT_FACE",FACE,{"disambiguationData":[OSD([sQuery(id+"F45.wireOp",EDGE,"E78.right")])]}),makeQuery(id+"F48.opExtrude","SWEPT_FACE",FACE,{"disambiguationData":[OSD([subQ0])]})]}),makeQuery(id+"F49.opExtrude","SWEPT_FACE",FACE,{"disambiguationData":[OSD([subQ0]),TDD([makeQuery(id+"F47.imprint","IMPRINT",EDGE,{"disambiguationData":[TD([[makeQuery(id+"F47.imprint","INTERSECT",VERTEX,{"derivedFrom":[makeQuery(id+"F46.opExtrude","CAP_EDGE",EDGE,{"disambiguationData":[OSD([subQ1])],"isStart":false}),subQ0]}),1.0]])],"derivedFrom":subQ0})])]}),makeQuery(id+"F49.opExtrude","SWEPT_FACE",FACE,{"disambiguationData":[OSD([subQ0]),TDD([makeQuery(id+"F47.imprint","IMPRINT",EDGE,{"disambiguationData":[TD([[makeQuery(id+"F47.imprint","INTERSECT",VERTEX,{"derivedFrom":[makeQuery(id+"F46.opExtrude","CAP_EDGE",EDGE,{"disambiguationData":[OSD([sQuery(id+"F45.wireOp",EDGE,"E78.top")])],"isStart":false}),subQ0]}),-1.0]])],"derivedFrom":subQ0})])]})]})]});}
            var Q1;
            Q1=makeQuery(id+"F48.opExtrude","CAP_EDGE",EDGE,{"disambiguationData":[OSD([sQuery(id+"F47.wireOp",EDGE,"E79.right")])],"isStart":false});
            var Q2;
            Q2=makeQuery(id+"F48.opExtrude","CAP_EDGE",EDGE,{"disambiguationData":[OSD([sQuery(id+"F45.wireOp",EDGE,"E78.top")])],"isStart":false});
            var Q3;
            Q3=makeQuery(id+"F48.opExtrude","CAP_EDGE",EDGE,{"disambiguationData":[OSD([sQuery(id+"F47.wireOp",EDGE,"E79.left")])],"isStart":false});
            var Q4;
            {var subQ0=sQuery(id+"F47.wireOp",EDGE,"E79.left");var subQ1=sQuery(id+"F45.wireOp",EDGE,"E78.bottom");Q4=makeQuery(id+"F52.opChamfer","BLEND_EDGE",EDGE,{"blendedFrom":[makeQuery(id+"F48.opExtrude","CAP_EDGE",EDGE,{"disambiguationData":[OSD([subQ1])],"isStart":false}),makeQuery(id+"F49.boolean.opBoolean","MERGE",FACE,{"derivedFrom":[makeQuery(id+"F48.boolean.opBoolean","MERGE",FACE,{"derivedFrom":[makeQuery(id+"F46.opExtrude","SWEPT_FACE",FACE,{"disambiguationData":[OSD([sQuery(id+"F45.wireOp",EDGE,"E78.left")])]}),makeQuery(id+"F48.opExtrude","SWEPT_FACE",FACE,{"disambiguationData":[OSD([subQ0])]})]}),makeQuery(id+"F49.opExtrude","SWEPT_FACE",FACE,{"disambiguationData":[OSD([subQ0]),TDD([makeQuery(id+"F47.imprint","IMPRINT",EDGE,{"disambiguationData":[TD([[makeQuery(id+"F47.imprint","INTERSECT",VERTEX,{"derivedFrom":[makeQuery(id+"F46.opExtrude","CAP_EDGE",EDGE,{"disambiguationData":[OSD([subQ1])],"isStart":false}),subQ0]}),1.0]])],"derivedFrom":subQ0})])]}),makeQuery(id+"F49.opExtrude","SWEPT_FACE",FACE,{"disambiguationData":[OSD([subQ0]),TDD([makeQuery(id+"F47.imprint","IMPRINT",EDGE,{"disambiguationData":[TD([[makeQuery(id+"F47.imprint","INTERSECT",VERTEX,{"derivedFrom":[makeQuery(id+"F46.opExtrude","CAP_EDGE",EDGE,{"disambiguationData":[OSD([sQuery(id+"F45.wireOp",EDGE,"E78.top")])],"isStart":false}),subQ0]}),-1.0]])],"derivedFrom":subQ0})])]})]})],"blendedInto":[makeQuery(id+"F49.boolean.opBoolean","MERGE",FACE,{"derivedFrom":[makeQuery(id+"F48.boolean.opBoolean","MERGE",FACE,{"derivedFrom":[makeQuery(id+"F46.opExtrude","SWEPT_FACE",FACE,{"disambiguationData":[OSD([sQuery(id+"F45.wireOp",EDGE,"E78.left")])]}),makeQuery(id+"F48.opExtrude","SWEPT_FACE",FACE,{"disambiguationData":[OSD([subQ0])]})]}),makeQuery(id+"F49.opExtrude","SWEPT_FACE",FACE,{"disambiguationData":[OSD([subQ0]),TDD([makeQuery(id+"F47.imprint","IMPRINT",EDGE,{"disambiguationData":[TD([[makeQuery(id+"F47.imprint","INTERSECT",VERTEX,{"derivedFrom":[makeQuery(id+"F46.opExtrude","CAP_EDGE",EDGE,{"disambiguationData":[OSD([subQ1])],"isStart":false}),subQ0]}),1.0]])],"derivedFrom":subQ0})])]}),makeQuery(id+"F49.opExtrude","SWEPT_FACE",FACE,{"disambiguationData":[OSD([subQ0]),TDD([makeQuery(id+"F47.imprint","IMPRINT",EDGE,{"disambiguationData":[TD([[makeQuery(id+"F47.imprint","INTERSECT",VERTEX,{"derivedFrom":[makeQuery(id+"F46.opExtrude","CAP_EDGE",EDGE,{"disambiguationData":[OSD([sQuery(id+"F45.wireOp",EDGE,"E78.top")])],"isStart":false}),subQ0]}),-1.0]])],"derivedFrom":subQ0})])]})]})]});}
            chamfer(context, id + "F53", {"entities" : qUnion([Q0, Q1, Q2, Q3, Q4]), "width" : 4 * mm, "tangentPropagation" : true});
        }
        {
            var Q0;
            {var subQ1=sQuery(id+"F45.wireOp",EDGE,"E78.right");var subQ2=sQuery(id+"F45.wireOp",EDGE,"E78.left");var subQ3=sQuery(id+"F45.wireOp",EDGE,"E78.top");var subQ4=sQuery(id+"F45.wireOp",EDGE,"E78.bottom");Q0=makeQuery(id+"F49.boolean.opBoolean","SPLIT",FACE,{"disambiguationData":[TD([makeQuery(id+"F46.opExtrude","CAP_FACE",FACE,{"disambiguationData":[OSD([subQ4,subQ3,subQ2,subQ1])],"isStart":true})])],"derivedFrom":makeQuery(id+"F48.boolean.opBoolean","MERGE",FACE,{"derivedFrom":[makeQuery(id+"F46.opExtrude","SWEPT_FACE",FACE,{"disambiguationData":[OSD([subQ3])]}),makeQuery(id+"F48.opExtrude","SWEPT_FACE",FACE,{"disambiguationData":[OSD([subQ3])]})]})});}
            var sketch = newSketch(context, id + "F54", { "sketchPlane" : qUnion([Q0])});
            skLineSegment(sketch, "E91.bottom", {"start": v(-33.71, 9) * mm, "end": v(-25.71, 9) * mm});
            skLineSegment(sketch, "E91.top", {"start": v(-33.71, 4) * mm, "end": v(-25.71, 4) * mm});
            skLineSegment(sketch, "E91.left", {"start": v(-33.71, 9) * mm, "end": v(-33.71, 4) * mm});
            skLineSegment(sketch, "E91.right", {"start": v(-25.71, 9) * mm, "end": v(-25.71, 4) * mm});
            skSolve(sketch);
        }
        {
            var Q0;
            Q0=makeQuery(id+"F54.imprint","IMPRINT",FACE,{"disambiguationData":[TD([[makeQuery(id+"F54.imprint","IMPRINT",EDGE,{"derivedFrom":sQuery(id+"F54.wireOp",EDGE,"E91.bottom")}),-1.0]])]});
            extrude(context, id + "F55", {"entities" : qUnion([Q0]), "operationType" : NewBodyOperationType.ADD, "depth" : 10 * mm, "offsetDistance" : 25 * mm});
        }
        {
            var Q0;
            Q0=qCreatedBy(makeId("Top.planeOp"),FACE);
            var sketch = newSketch(context, id + "F56", { "sketchPlane" : qUnion([Q0])});
            skLineSegment(sketch, "E92.bottom", {"start": v(92.03, -69.54) * mm, "end": v(121.53, -69.54) * mm});
            skLineSegment(sketch, "E92.top", {"start": v(92.03, -9.54) * mm, "end": v(121.53, -9.54) * mm});
            skLineSegment(sketch, "E92.left", {"start": v(92.03, -69.54) * mm, "end": v(92.03, -9.54) * mm});
            skLineSegment(sketch, "E92.right", {"start": v(121.53, -69.54) * mm, "end": v(121.53, -9.54) * mm});
            skSolve(sketch);
        }
        {
            var Q0;
            Q0=makeQuery(id+"F56.imprint","IMPRINT",FACE,{"disambiguationData":[TD([[makeQuery(id+"F56.imprint","IMPRINT",EDGE,{"derivedFrom":sQuery(id+"F56.wireOp",EDGE,"E92.bottom")}),1.0]])]});
            extrude(context, id + "F57", {"entities" : qUnion([Q0]), "depth" : 41 * mm, "offsetDistance" : 25 * mm});
        }
        {
            var Q0;
            Q0=makeQuery(id+"F57.opExtrude","CAP_FACE",FACE,{"disambiguationData":[OSD([sQuery(id+"F56.wireOp",EDGE,"E92.bottom"),sQuery(id+"F56.wireOp",EDGE,"E92.top"),sQuery(id+"F56.wireOp",EDGE,"E92.left"),sQuery(id+"F56.wireOp",EDGE,"E92.right")])],"isStart":false});
            var sketch = newSketch(context, id + "F58", { "sketchPlane" : qUnion([Q0])});
            skLineSegment(sketch, "E93.bottom", {"start": v(92.03, -77.54) * mm, "end": v(121.53, -77.54) * mm});
            skLineSegment(sketch, "E93.top", {"start": v(92.03, -1.54) * mm, "end": v(121.53, -1.54) * mm});
            skLineSegment(sketch, "E93.left", {"start": v(92.03, -77.54) * mm, "end": v(92.03, -1.54) * mm});
            skLineSegment(sketch, "E93.right", {"start": v(121.53, -77.54) * mm, "end": v(121.53, -1.54) * mm});
            skCircle(sketch, "E94", {"center": v(97.53, -5.29) * mm, "radius": 2.5 * mm});
            skCircle(sketch, "E95", {"center": v(116.03, -5.29) * mm, "radius": 2.5 * mm});
            skCircle(sketch, "E96", {"center": v(97.53, -73.79) * mm, "radius": 2.5 * mm});
            skCircle(sketch, "E97", {"center": v(116.03, -73.79) * mm, "radius": 2.5 * mm});
            skLineSegment(sketch, "E98", {"start": v(97.53, -5.29) * mm, "end": v(97.53, -73.79) * mm, "construction": true});
            skLineSegment(sketch, "E99", {"start": v(116.03, -73.79) * mm, "end": v(97.53, -73.79) * mm, "construction": true});
            skLineSegment(sketch, "E100", {"start": v(116.03, -5.29) * mm, "end": v(97.53, -5.29) * mm, "construction": true});
            skLineSegment(sketch, "E101", {"start": v(116.03, -5.29) * mm, "end": v(116.03, -73.79) * mm, "construction": true});
            skSolve(sketch);
        }
        {
            var Q0;
            {var subQ1=makeQuery(id+"F57.opExtrude","CAP_EDGE",EDGE,{"disambiguationData":[OSD([sQuery(id+"F56.wireOp",EDGE,"E92.bottom")])],"isStart":false});Q0=makeQuery(id+"F58.imprint","IMPRINT",FACE,{"disambiguationData":[TD([[makeQuery(id+"F58.imprint","IMPRINT",EDGE,{"derivedFrom":subQ1}),1.0]])]});}
            extrude(context, id + "F59", {"entities" : qUnion([Q0]), "operationType" : NewBodyOperationType.ADD, "depth" : 6.5 * mm, "offsetDistance" : 25 * mm});
        }
        {
            var Q0;
            {var subQ2=sQuery(id+"F58.wireOp",EDGE,"E93.bottom");Q0=makeQuery(id+"F58.imprint","IMPRINT",FACE,{"disambiguationData":[TD([[makeQuery(id+"F58.imprint","IMPRINT",EDGE,{"derivedFrom":subQ2}),1.0]])]});}
            var Q1;
            {var subQ2=sQuery(id+"F58.wireOp",EDGE,"E93.top");Q1=makeQuery(id+"F58.imprint","IMPRINT",FACE,{"disambiguationData":[TD([[makeQuery(id+"F58.imprint","IMPRINT",EDGE,{"derivedFrom":subQ2}),-1.0]])]});}
            extrude(context, id + "F60", {"entities" : qUnion([Q0, Q1]), "operationType" : NewBodyOperationType.ADD, "depth" : 4 * mm, "offsetDistance" : 25 * mm});
        }
        {
            var Q0;
            Q0=makeQuery(id+"F59.opExtrude","CAP_FACE",FACE,{"disambiguationData":[OSD([sQuery(id+"F56.wireOp",EDGE,"E92.bottom"),sQuery(id+"F56.wireOp",EDGE,"E92.top"),sQuery(id+"F58.wireOp",EDGE,"E93.left"),sQuery(id+"F58.wireOp",EDGE,"E93.right")])],"isStart":false});
            var sketch = newSketch(context, id + "F61", { "sketchPlane" : qUnion([Q0])});
            skArc(sketch, "E102", {"start": v(92.03, -54.79) * mm, "mid": v(106.78, -69.54) * mm, "end": v(121.53, -54.79) * mm});
            skLineSegment(sketch, "E103", {"start": v(106.78, -69.54) * mm, "end": v(106.78, -9.54) * mm, "construction": true});
            skLineSegment(sketch, "E104", {"start": v(106.78, -54.79) * mm, "end": v(92.03, -54.79) * mm, "construction": true});
            skLineSegment(sketch, "E105", {"start": v(106.78, -54.79) * mm, "end": v(121.53, -54.79) * mm, "construction": true});
            skLineSegment(sketch, "E106", {"start": v(92.03, -20.54) * mm, "end": v(121.53, -20.54) * mm});
            skSolve(sketch);
        }
        {
            var Q0;
            {var subQ0=sQuery(id+"F61.wireOp",EDGE,"E106");Q0=makeQuery(id+"F61.imprint","IMPRINT",FACE,{"disambiguationData":[TD([[makeQuery(id+"F61.imprint","IMPRINT",EDGE,{"derivedFrom":subQ0}),-1.0]])]});}
            extrude(context, id + "F62", {"entities" : qUnion([Q0]), "operationType" : NewBodyOperationType.ADD, "depth" : 3 * mm, "offsetDistance" : 25 * mm});
        }
        {
            var Q0;
            Q0=makeQuery(id+"F62.opExtrude","CAP_FACE",FACE,{"disambiguationData":[OSD([sQuery(id+"F58.wireOp",EDGE,"E93.left"),sQuery(id+"F58.wireOp",EDGE,"E93.right"),sQuery(id+"F61.wireOp",EDGE,"E102"),sQuery(id+"F61.wireOp",EDGE,"E106")])],"isStart":false});
            var sketch = newSketch(context, id + "F63", { "sketchPlane" : qUnion([Q0])});
            skCircle(sketch, "E107", {"center": v(106.78, -54.79) * mm, "radius": 9.5 * mm});
            skSolve(sketch);
        }
        {
            var Q0;
            Q0=makeQuery(id+"F63.imprint","IMPRINT",FACE,{"disambiguationData":[TD([[makeQuery(id+"F63.imprint","IMPRINT",EDGE,{"derivedFrom":sQuery(id+"F63.wireOp",EDGE,"E107")}),1.0]])]});
            extrude(context, id + "F64", {"entities" : qUnion([Q0]), "operationType" : NewBodyOperationType.ADD, "depth" : 3 * mm, "offsetDistance" : 25 * mm});
        }
        {
            var Q0;
            Q0=makeQuery(id+"F64.opExtrude","CAP_FACE",FACE,{"disambiguationData":[OSD([sQuery(id+"F63.wireOp",EDGE,"E107")])],"isStart":false});
            var sketch = newSketch(context, id + "F65", { "sketchPlane" : qUnion([Q0])});
            skCircle(sketch, "E108", {"center": v(106.78, -54.79) * mm, "radius": 4.25 * mm});
            skSolve(sketch);
        }
        {
            var Q0;
            Q0=makeQuery(id+"F65.imprint","IMPRINT",FACE,{"disambiguationData":[TD([[makeQuery(id+"F65.imprint","IMPRINT",EDGE,{"derivedFrom":sQuery(id+"F65.wireOp",EDGE,"E108")}),1.0]])]});
            extrude(context, id + "F66", {"entities" : qUnion([Q0]), "operationType" : NewBodyOperationType.ADD, "depth" : 5.5 * mm, "offsetDistance" : 25 * mm});
        }
        {
            var Q0;
            {var subQ0=sQuery(id+"F56.wireOp",EDGE,"E92.right");var subQ2=sQuery(id+"F56.wireOp",EDGE,"E92.left");var subQ3=sQuery(id+"F56.wireOp",EDGE,"E92.top");var subQ4=sQuery(id+"F56.wireOp",EDGE,"E92.bottom");Q0=makeQuery(id+"F60.boolean.opBoolean","SPLIT",FACE,{"disambiguationData":[TD([makeQuery(id+"F57.opExtrude","CAP_FACE",FACE,{"disambiguationData":[OSD([subQ4,subQ3,subQ2,subQ0])],"isStart":true})])],"derivedFrom":makeQuery(id+"F59.boolean.opBoolean","MERGE",FACE,{"derivedFrom":[makeQuery(id+"F57.opExtrude","SWEPT_FACE",FACE,{"disambiguationData":[OSD([subQ4])]}),makeQuery(id+"F59.opExtrude","SWEPT_FACE",FACE,{"disambiguationData":[OSD([subQ4])]})]})});}
            var sketch = newSketch(context, id + "F67", { "sketchPlane" : qUnion([Q0])});
            skLineSegment(sketch, "E109.bottom", {"start": v(103.28, 9) * mm, "end": v(110.28, 9) * mm});
            skLineSegment(sketch, "E109.top", {"start": v(103.28, 5) * mm, "end": v(110.28, 5) * mm});
            skLineSegment(sketch, "E109.left", {"start": v(103.28, 9) * mm, "end": v(103.28, 5) * mm});
            skLineSegment(sketch, "E109.right", {"start": v(110.28, 9) * mm, "end": v(110.28, 5) * mm});
            skLineSegment(sketch, "E110", {"start": v(106.78, 0) * mm, "end": v(106.78, 9) * mm, "construction": true});
            skSolve(sketch);
        }
        {
            var Q0;
            Q0=makeQuery(id+"F67.imprint","IMPRINT",FACE,{"disambiguationData":[TD([[makeQuery(id+"F67.imprint","IMPRINT",EDGE,{"derivedFrom":sQuery(id+"F67.wireOp",EDGE,"E109.bottom")}),-1.0]])]});
            extrude(context, id + "F68", {"entities" : qUnion([Q0]), "operationType" : NewBodyOperationType.ADD, "depth" : 10 * mm, "offsetDistance" : 25 * mm});
        }
    });
